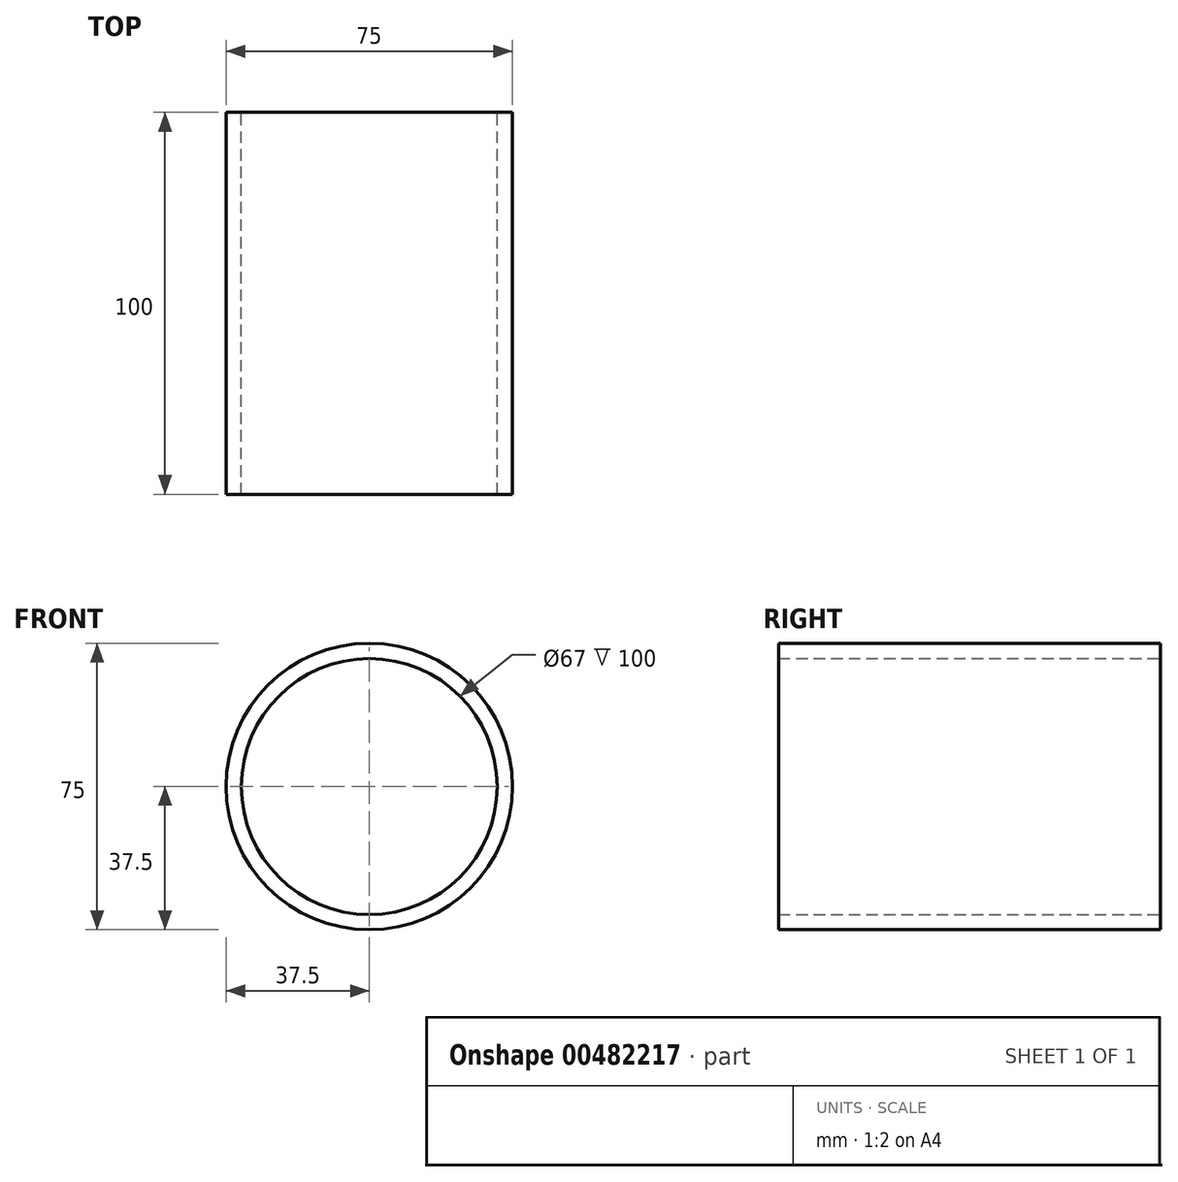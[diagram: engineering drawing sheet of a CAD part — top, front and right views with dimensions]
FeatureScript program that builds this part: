
annotation { "Feature Type Name" : "Feature", "Feature Type Description" : "" }
export const myFeature = defineFeature(function(context is Context, id is Id, definition is map)
    precondition{}
    {
        {
            var Q0;
            Q0=qCreatedBy(makeId("Front.planeOp"),FACE);
            var sketch = newSketch(context, id + "F0", { "sketchPlane" : qUnion([Q0])});
            skCircle(sketch, "E0", {"center": v(0, 0) * mm, "radius": 33.5 * mm});
            skCircle(sketch, "E1", {"center": v(0, 0) * mm, "radius": 37.5 * mm});
            skSolve(sketch);
        }
        {
            var Q0;
            Q0=makeQuery(id+"F0.imprint","IMPRINT",FACE,{"disambiguationData":[TD([[makeQuery(id+"F0.imprint","IMPRINT",EDGE,{"derivedFrom":sQuery(id+"F0.wireOp",EDGE,"E0")}),-1.0]])]});
            extrude(context, id + "F1", {"entities" : qUnion([Q0]), "depth" : 100 * mm, "offsetDistance" : 25 * mm});
        }
    });
